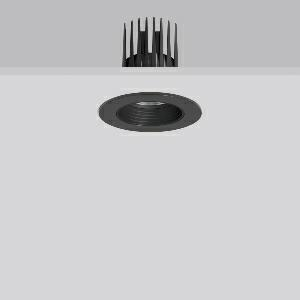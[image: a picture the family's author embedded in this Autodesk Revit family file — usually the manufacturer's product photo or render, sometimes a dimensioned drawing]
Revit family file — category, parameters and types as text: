
# Revit family: heledon_mini_e_901753_003_1_76_1bf2
name_source: partatom
category: Lighting Fixtures
units: mm (PartAtom-declared; Revit-internal decimal feet)

## family parameters
Cut with Voids When Loaded = No
Host = Face
Light Source = No
Part Type = Normal
Room Calculation Point = No
Round Connector Dimension = Use Diameter
Shared = No

## types (1)
- HELEDON mini E (1 x LED Modul 940, 3000 lm, 4000)
    Apparent Load = 29 VA
    Approval mark = CE
    CIE Flux Codes = 98 100 100 100 100
    Color Rendering = 92
    Color Temperature = 4000
    Default Elevation = 1800 mm
    Description = Series: HELEDON mini
Round recessed downlight. Housing: die-cast aluminium, powder-coated. Black plastic ring and recessed LED to prevent glare from the side. Optical assembly with lens made of plastic (polycarbonate) for the best homogeneous light distribution - can be changed without tools. Best colour rendering index Ra>90. Suitable for Recessed ceiling mounting. Installation without tools thanks to spring fastening system. Including separate LED converter with connecting cable 600 mm.High quality converter without flickering and stroboscopic effect. Through-wiring box (5 pole) available as accessory. The following accessories can be mounted without use of tools: interchangeable lenses, decorative glasses, honeycomb louvre, clear and frosted diffusers, white interchangeable plastic ring. 
Colour: deep black, matt (RAL 9005)
Diameter: 124 mm
Height: 3 mm
Cut-out diameter: 114 mm
Recess height: 170 mm
Luminaire: recess height: 120 mm
Lamp: LED
Socket: without socket
Colour temperature: 4000K
Colour rendering index (CRI): 92
System power: 29 W
Rated luminous flux: 3000 lm
Luminous efficiency: 103 lm/W
Control gear: Converter, dimmable, DALI
Protection class: II
Type of protection: IP 20
    Height = 0 mm  [stored 0 ft]
    Lamp = 1 x LED Modul 940
    Lamp Light Flux = 3000 lm
    Lamp count = 1
    Length = 124 mm  [stored 0.406824 ft]
    Lifetime = 50000 h
    Luminous efficacy = 103 lm/W
    Manufacturer = RZB
    ModVariant = No
    Model = 901753.003.1.76
    Mounting Place = Ceiling
    Mounting Type = Recessed
    Number of Poles = 1
    OnlyDefault = Yes
    Power Factor = 1
    Product Name = HELEDON mini E
    Product group = Recessed downlights
    ProductGroupID = 402
    Protection Class = Protection class II
    Protection Degree = IP 20
    RLX_Detail_Level = 1
    RLX_Emergency_Light_Flux = 0 lm
    RLX_Emergency_Type = 0
    RLX_Emergency_Type_DB = No
    RlxData = <blob elided: 125121 chars, md5=490cac09>
    Socket = socket
    Standby Power = 0 W
    System Light Flux = 3000 lm
    System Power = 29 W
    Type Comments = Product without accessories
    Type Image = 901656.003.jpg
    URL = http://relux.com
    VarID = ---
    Voltage = 230 V
    Voltage Range = 220-240 V
    Weight = 0.00 kg
    Width = 0 mm  [stored 0 ft]

note: [stored X ft] marks values corroborated as IEEE doubles in the binary element streams (Revit-internal decimal feet)

## geometry (parser evidence)
native form markers: Blend x4, Sweep x12
no freeform markers — native parametric forms only
